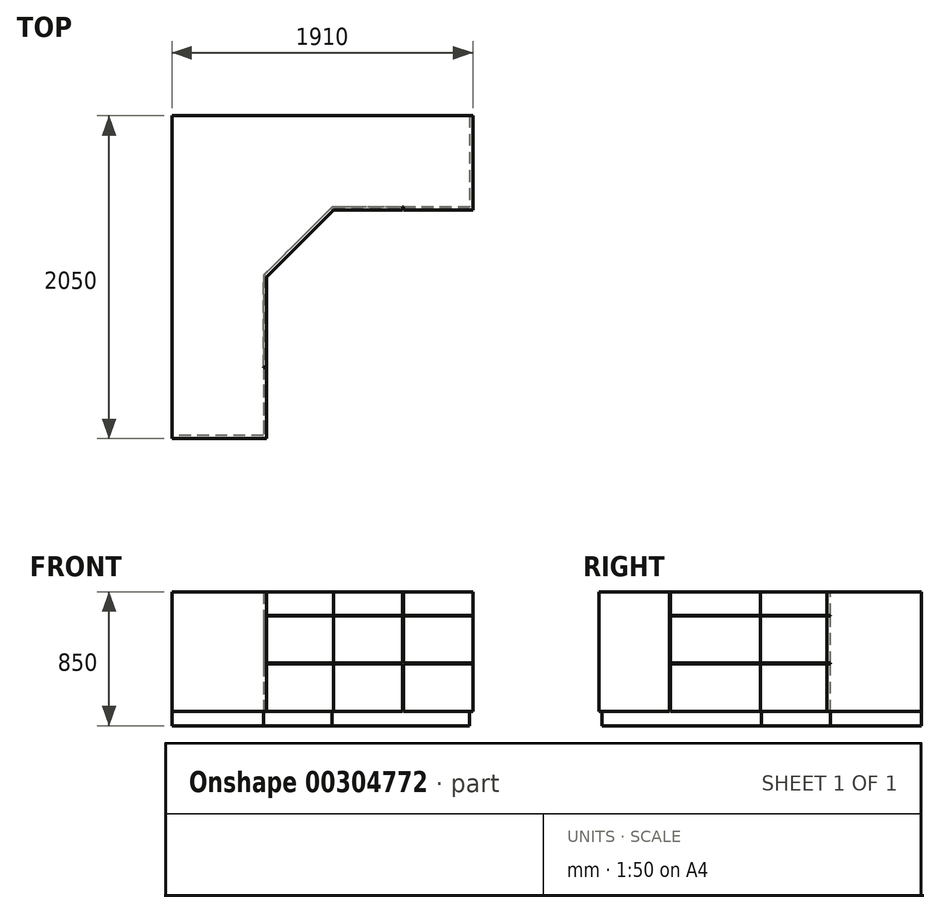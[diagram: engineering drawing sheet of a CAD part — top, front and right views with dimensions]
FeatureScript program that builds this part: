
annotation { "Feature Type Name" : "Feature", "Feature Type Description" : "" }
export const myFeature = defineFeature(function(context is Context, id is Id, definition is map)
    precondition{}
    {
        {
            var Q0;
            Q0=qCreatedBy(makeId("Top.planeOp"),FACE);
            var sketch = newSketch(context, id + "F0", { "sketchPlane" : qUnion([Q0])});
            skLineSegment(sketch, "E0", {"start": v(-993.67, -939.37) * mm, "end": v(-993.67, 1110.63) * mm});
            skLineSegment(sketch, "E1", {"start": v(-993.67, 1110.63) * mm, "end": v(916.33, 1110.63) * mm});
            skLineSegment(sketch, "E2", {"start": v(916.33, 1110.63) * mm, "end": v(916.33, 510.63) * mm});
            skLineSegment(sketch, "E3", {"start": v(916.33, 510.63) * mm, "end": v(30.6, 510.63) * mm});
            skLineSegment(sketch, "E4", {"start": v(30.6, 510.63) * mm, "end": v(-393.67, 86.36) * mm});
            skLineSegment(sketch, "E5", {"start": v(-393.67, 86.36) * mm, "end": v(-393.67, -939.37) * mm});
            skLineSegment(sketch, "E6", {"start": v(-393.67, -939.37) * mm, "end": v(-993.67, -939.37) * mm});
            skSolve(sketch);
        }
        {
            var Q0;
            Q0=makeQuery(id+"F0.imprint","IMPRINT",FACE,{"disambiguationData":[TD([[makeQuery(id+"F0.imprint","IMPRINT",EDGE,{"derivedFrom":sQuery(id+"F0.wireOp",EDGE,"E0")}),-1.0]])]});
            extrude(context, id + "F1", {"entities" : qUnion([Q0]), "depth" : 850 * mm});
        }
        {
            var Q0;
            Q0=makeQuery(id+"F1.opExtrude","CAP_FACE",FACE,{"disambiguationData":[OSD([sQuery(id+"F0.wireOp",EDGE,"E0"),sQuery(id+"F0.wireOp",EDGE,"E1"),sQuery(id+"F0.wireOp",EDGE,"E2"),sQuery(id+"F0.wireOp",EDGE,"E3"),sQuery(id+"F0.wireOp",EDGE,"E4"),sQuery(id+"F0.wireOp",EDGE,"E5"),sQuery(id+"F0.wireOp",EDGE,"E6")])],"isStart":true});
            var sketch = newSketch(context, id + "F2", { "sketchPlane" : qUnion([Q0])});
            skLineSegment(sketch, "E7.0", {"start": v(-413.67, 919.37) * mm, "end": v(-993.67, 919.37) * mm});
            skLineSegment(sketch, "E7.1", {"start": v(896.33, -1110.63) * mm, "end": v(896.33, -530.63) * mm});
            skLineSegment(sketch, "E7.2", {"start": v(896.33, -530.63) * mm, "end": v(22.31, -530.63) * mm});
            skLineSegment(sketch, "E7.3", {"start": v(22.31, -530.63) * mm, "end": v(-413.67, -94.65) * mm});
            skLineSegment(sketch, "E7.4", {"start": v(-413.67, -94.65) * mm, "end": v(-413.67, 919.37) * mm});
            skLineSegment(sketch, "E8.0", {"start": v(-993.67, 939.37) * mm, "end": v(-993.67, 919.37) * mm});
            skLineSegment(sketch, "E9.0", {"start": v(-393.67, 939.37) * mm, "end": v(-993.67, 939.37) * mm});
            skLineSegment(sketch, "E10.0", {"start": v(-393.67, -86.36) * mm, "end": v(-393.67, 939.37) * mm});
            skLineSegment(sketch, "E11.0", {"start": v(30.6, -510.63) * mm, "end": v(-393.67, -86.36) * mm});
            skLineSegment(sketch, "E12.0", {"start": v(916.33, -510.63) * mm, "end": v(30.6, -510.63) * mm});
            skLineSegment(sketch, "E13.0", {"start": v(916.33, -1110.63) * mm, "end": v(916.33, -510.63) * mm});
            skLineSegment(sketch, "E14.0", {"start": v(896.33, -1110.63) * mm, "end": v(916.33, -1110.63) * mm});
            skPoint(sketch, "E15.orphan", {"position": v(-993.67, -1110.63) * mm});
            skSolve(sketch);
        }
        {
            var Q0;
            Q0 = qSketchRegion(id + "F2", true);
            extrude(context, id + "F3", {"entities" : qUnion([Q0]), "operationType" : NewBodyOperationType.REMOVE, "oppositeDirection" : true, "depth" : 90 * mm});
        }
        {
            var Q0;
            Q0=makeQuery(id+"F1.opExtrude","SWEPT_FACE",FACE,{"disambiguationData":[OSD([sQuery(id+"F0.wireOp",EDGE,"E5")])]});
            var sketch = newSketch(context, id + "F4", { "sketchPlane" : qUnion([Q0])});
            skLineSegment(sketch, "E16.0", {"start": v(86.36, 850) * mm, "end": v(-489.37, 850) * mm});
            skLineSegment(sketch, "E17.0", {"start": v(86.36, 90) * mm, "end": v(-489.37, 90) * mm});
            skLineSegment(sketch, "E18", {"start": v(-489.37, 850) * mm, "end": v(-489.37, 90) * mm});
            skLineSegment(sketch, "E19", {"start": v(-484.37, 850) * mm, "end": v(-484.37, 90) * mm});
            skLineSegment(sketch, "E20", {"start": v(-484.37, 90) * mm, "end": v(-489.37, 90) * mm});
            skLineSegment(sketch, "E21", {"start": v(-489.37, 850) * mm, "end": v(-484.37, 850) * mm});
            skPoint(sketch, "E22.orphan", {"position": v(-939.37, 850) * mm});
            skPoint(sketch, "E23.orphan", {"position": v(-939.37, 90) * mm});
            skSolve(sketch);
        }
        {
            var Q0;
            Q0=makeQuery(id+"F4.imprint","IMPRINT",FACE,{"disambiguationData":[TD([[makeQuery(id+"F4.imprint","IMPRINT",EDGE,{"derivedFrom":sQuery(id+"F4.wireOp",EDGE,"E18")}),1.0]])]});
            extrude(context, id + "F5", {"entities" : qUnion([Q0]), "operationType" : NewBodyOperationType.REMOVE, "oppositeDirection" : true, "offsetDistance" : 25 * mm, "depth" : 20 * mm});
        }
        {
            var Q0;
            Q0=makeQuery(id+"F1.opExtrude","SWEPT_FACE",FACE,{"disambiguationData":[OSD([sQuery(id+"F0.wireOp",EDGE,"E3")])]});
            var sketch = newSketch(context, id + "F6", { "sketchPlane" : qUnion([Q0])});
            skLineSegment(sketch, "E24.0", {"start": v(30.6, 702.5) * mm, "end": v(30.6, 697.5) * mm});
            skLineSegment(sketch, "E25.0", {"start": v(475.96, 850) * mm, "end": v(470.96, 850) * mm});
            skLineSegment(sketch, "E26.0", {"start": v(916.33, 702.5) * mm, "end": v(916.33, 697.5) * mm});
            skLineSegment(sketch, "E27.0", {"start": v(475.96, 90) * mm, "end": v(470.96, 90) * mm});
            skPoint(sketch, "E28", {"position": v(473.46, 850) * mm});
            skPoint(sketch, "E29", {"position": v(473.46, 90) * mm});
            skLineSegment(sketch, "E30", {"start": v(473.46, 850) * mm, "end": v(473.46, 90) * mm, "construction": true});
            skLineSegment(sketch, "E31", {"start": v(470.96, 850) * mm, "end": v(470.96, 702.5) * mm});
            skLineSegment(sketch, "E32", {"start": v(475.96, 90) * mm, "end": v(475.96, 393.75) * mm});
            skLineSegment(sketch, "E33", {"start": v(30.6, 700) * mm, "end": v(916.33, 700) * mm, "construction": true});
            skLineSegment(sketch, "E34", {"start": v(30.6, 702.5) * mm, "end": v(470.96, 702.5) * mm});
            skLineSegment(sketch, "E35", {"start": v(30.6, 697.5) * mm, "end": v(470.96, 697.5) * mm});
            skLineSegment(sketch, "E36.trimOffspring", {"start": v(475.96, 702.5) * mm, "end": v(916.33, 702.5) * mm});
            skLineSegment(sketch, "E37.trimOffspring", {"start": v(475.96, 702.5) * mm, "end": v(475.96, 850) * mm});
            skLineSegment(sketch, "E38.trimOffspring", {"start": v(470.96, 697.5) * mm, "end": v(470.96, 398.75) * mm});
            skLineSegment(sketch, "E39.trimOffspring", {"start": v(475.96, 697.5) * mm, "end": v(916.33, 697.5) * mm});
            skPoint(sketch, "E40.orphan", {"position": v(30.6, 850) * mm});
            skPoint(sketch, "E41.orphan", {"position": v(916.33, 850) * mm});
            skLineSegment(sketch, "E42", {"start": v(30.6, 396.25) * mm, "end": v(916.33, 396.25) * mm, "construction": true});
            skLineSegment(sketch, "E43", {"start": v(30.6, 398.75) * mm, "end": v(470.96, 398.75) * mm});
            skLineSegment(sketch, "E44", {"start": v(30.6, 393.75) * mm, "end": v(470.96, 393.75) * mm});
            skLineSegment(sketch, "E45.trimOffspring", {"start": v(30.6, 398.75) * mm, "end": v(30.6, 393.75) * mm});
            skLineSegment(sketch, "E46.trimOffspring", {"start": v(475.96, 398.75) * mm, "end": v(916.33, 398.75) * mm});
            skLineSegment(sketch, "E47.trimOffspring", {"start": v(470.96, 393.75) * mm, "end": v(470.96, 90) * mm});
            skLineSegment(sketch, "E48.trimOffspring", {"start": v(475.96, 393.75) * mm, "end": v(916.33, 393.75) * mm});
            skLineSegment(sketch, "E49.trimOffspring", {"start": v(475.96, 398.75) * mm, "end": v(475.96, 697.5) * mm});
            skPoint(sketch, "E50.orphan", {"position": v(30.6, 90) * mm});
            skPoint(sketch, "E51.orphan", {"position": v(916.33, 90) * mm});
            skLineSegment(sketch, "E52.trimOffspring", {"start": v(916.33, 398.75) * mm, "end": v(916.33, 393.75) * mm});
            skSolve(sketch);
        }
        {
            var Q0;
            Q0=makeQuery(id+"F6.imprint","IMPRINT",FACE,{"disambiguationData":[TD([[makeQuery(id+"F6.imprint","IMPRINT",EDGE,{"derivedFrom":sQuery(id+"F6.wireOp",EDGE,"E24.0")}),1.0]])]});
            extrude(context, id + "F7", {"entities" : qUnion([Q0]), "operationType" : NewBodyOperationType.REMOVE, "oppositeDirection" : true, "depth" : 20 * mm});
        }
        {
            var Q0;
            {var subQ0=sQuery(id+"F0.wireOp",EDGE,"E5");var subQ1=sQuery(id+"F0.wireOp",EDGE,"E4");Q0=makeQuery(id+"F5.boolean.opBoolean","SPLIT",FACE,{"disambiguationData":[TD([makeQuery(id+"F1.opExtrude","SWEPT_FACE",FACE,{"disambiguationData":[OSD([subQ1])]})])],"derivedFrom":makeQuery(id+"F1.opExtrude","SWEPT_FACE",FACE,{"disambiguationData":[OSD([subQ0])]})});}
            var sketch = newSketch(context, id + "F8", { "sketchPlane" : qUnion([Q0])});
            skLineSegment(sketch, "E53.0", {"start": v(-484.37, 850) * mm, "end": v(-484.37, 697.5) * mm});
            skLineSegment(sketch, "E54.0", {"start": v(86.36, 850) * mm, "end": v(86.36, 697.5) * mm});
            skLineSegment(sketch, "E55", {"start": v(-484.37, 700) * mm, "end": v(86.36, 700) * mm, "construction": true});
            skLineSegment(sketch, "E56", {"start": v(-484.37, 702.5) * mm, "end": v(86.36, 702.5) * mm});
            skLineSegment(sketch, "E57", {"start": v(-484.37, 697.5) * mm, "end": v(86.36, 697.5) * mm});
            skLineSegment(sketch, "E58", {"start": v(-484.37, 398.75) * mm, "end": v(86.36, 398.75) * mm});
            skLineSegment(sketch, "E59", {"start": v(-484.37, 393.75) * mm, "end": v(86.36, 393.75) * mm});
            skPoint(sketch, "E60.orphan", {"position": v(-484.37, 90) * mm});
            skPoint(sketch, "E61.orphan", {"position": v(86.36, 90) * mm});
            skLineSegment(sketch, "E62", {"start": v(-484.37, 398.75) * mm, "end": v(-484.37, 393.75) * mm});
            skLineSegment(sketch, "E63", {"start": v(86.36, 398.75) * mm, "end": v(86.36, 393.75) * mm});
            skLineSegment(sketch, "E64.0", {"start": v(530.63, 398.75) * mm, "end": v(510.63, 398.75) * mm});
            skSolve(sketch);
        }
        {
            var Q0;
            {var subQ2=sQuery(id+"F8.wireOp",EDGE,"E56");Q0=makeQuery(id+"F8.imprint","IMPRINT",FACE,{"disambiguationData":[TD([[makeQuery(id+"F8.imprint","IMPRINT",EDGE,{"derivedFrom":subQ2}),-1.0]])]});}
            var Q1;
            Q1=makeQuery(id+"F8.imprint","IMPRINT",FACE,{"disambiguationData":[TD([[makeQuery(id+"F8.imprint","IMPRINT",EDGE,{"derivedFrom":sQuery(id+"F8.wireOp",EDGE,"E58")}),-1.0]])]});
            extrude(context, id + "F9", {"entities" : qUnion([Q0, Q1]), "operationType" : NewBodyOperationType.REMOVE, "oppositeDirection" : true, "depth" : 20 * mm});
        }
        {
            var Q0;
            Q0=makeQuery(id+"F1.opExtrude","SWEPT_FACE",FACE,{"disambiguationData":[OSD([sQuery(id+"F0.wireOp",EDGE,"E4")])]});
            var sketch = newSketch(context, id + "F10", { "sketchPlane" : qUnion([Q0])});
            skLineSegment(sketch, "E65.0", {"start": v(-217.3, 702.5) * mm, "end": v(-217.3, 697.5) * mm});
            skLineSegment(sketch, "E66.0", {"start": v(382.7, 702.5) * mm, "end": v(382.7, 697.5) * mm});
            skLineSegment(sketch, "E67.0", {"start": v(-217.3, 398.75) * mm, "end": v(-217.3, 393.75) * mm});
            skLineSegment(sketch, "E68.0", {"start": v(382.7, 398.75) * mm, "end": v(382.7, 393.75) * mm});
            skLineSegment(sketch, "E69", {"start": v(-217.3, 398.75) * mm, "end": v(382.7, 398.75) * mm});
            skLineSegment(sketch, "E70", {"start": v(382.7, 393.75) * mm, "end": v(-217.3, 393.75) * mm});
            skLineSegment(sketch, "E71", {"start": v(-217.3, 697.5) * mm, "end": v(382.7, 697.5) * mm});
            skLineSegment(sketch, "E72", {"start": v(-217.3, 702.5) * mm, "end": v(382.7, 702.5) * mm});
            skSolve(sketch);
        }
        {
            var Q0;
            Q0=makeQuery(id+"F10.imprint","IMPRINT",FACE,{"disambiguationData":[TD([[makeQuery(id+"F10.imprint","IMPRINT",EDGE,{"derivedFrom":sQuery(id+"F10.wireOp",EDGE,"E65.0")}),1.0]])]});
            var Q1;
            Q1=makeQuery(id+"F10.imprint","IMPRINT",FACE,{"disambiguationData":[TD([[makeQuery(id+"F10.imprint","IMPRINT",EDGE,{"derivedFrom":sQuery(id+"F10.wireOp",EDGE,"E67.0")}),1.0]])]});
            extrude(context, id + "F11", {"entities" : qUnion([Q0, Q1]), "operationType" : NewBodyOperationType.REMOVE, "oppositeDirection" : true, "depth" : 20 * mm});
        }
    });
